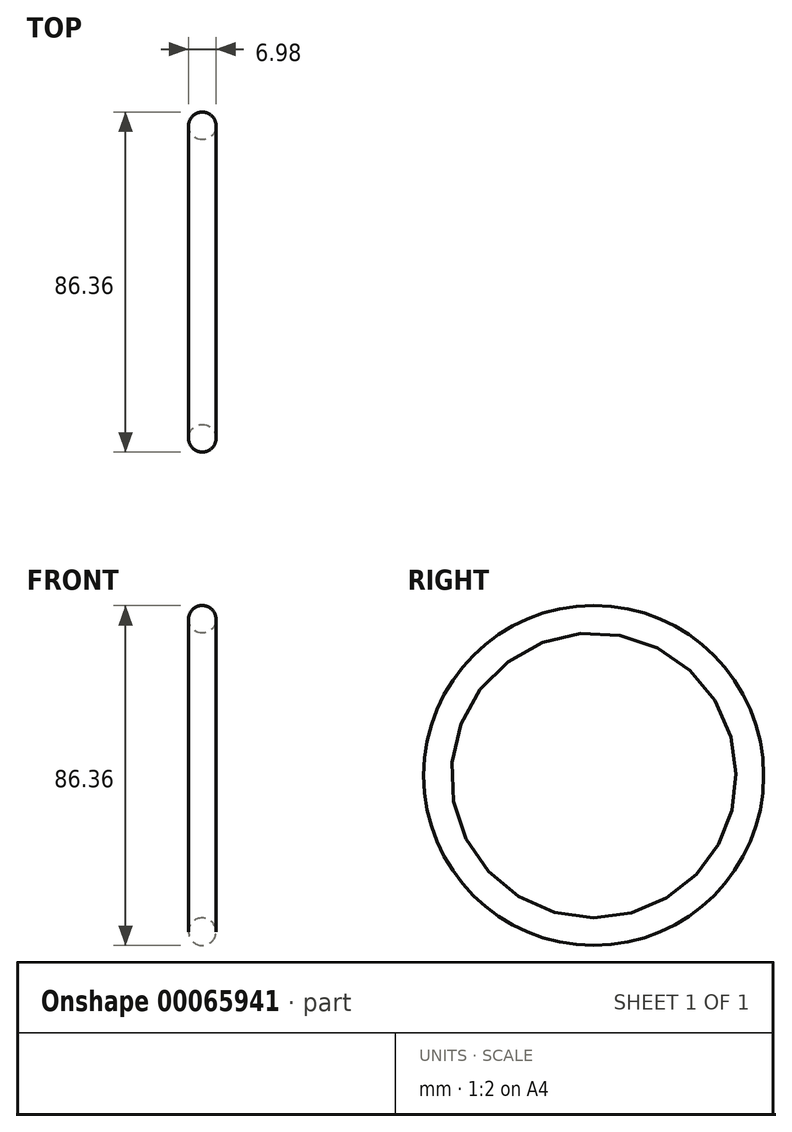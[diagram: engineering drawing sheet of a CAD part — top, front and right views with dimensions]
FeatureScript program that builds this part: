
annotation { "Feature Type Name" : "Feature", "Feature Type Description" : "" }
export const myFeature = defineFeature(function(context is Context, id is Id, definition is map)
    precondition{}
    {
        {
            var Q0;
            Q0=qCreatedBy(makeId("Front.planeOp"),FACE);
            var sketch = newSketch(context, id + "F0", { "sketchPlane" : qUnion([Q0])});
            skLineSegment(sketch, "E0", {"start": v(0, 0) * mm, "end": v(-6.06, 0) * mm, "construction": true});
            skCircle(sketch, "E1", {"center": v(0, 39.69) * mm, "radius": 3.5 * mm});
            skSolve(sketch);
        }
        {
            var Q0;
            Q0=makeQuery(id+"F0.imprint","IMPRINT",FACE,{"disambiguationData":[TD([[makeQuery(id+"F0.imprint","IMPRINT",EDGE,{"derivedFrom":sQuery(id+"F0.wireOp",EDGE,"E1")}),1.0]])]});
            var Q1;
            Q1=sQuery(id+"F0.wireOp",EDGE,"E0");
            revolve(context, id + "F1", {"entities" : qUnion([Q0]), "axis" : qUnion([Q1]), "revolveType" : RevolveType.FULL});
        }
    });
